# Revit family: STH7085_27
name_source: partatom
category: Luminárias
units: mm (PartAtom-declared; Revit-internal decimal feet)

## family parameters
Com base no plano de trabalho = Não
Compartilhado = Não
Corte com vazios quando carregada = Não
Cota do conector redondo = Utilizar diâmetro
Fonte luminosa = Sim
Manter orientação da anotação = Não
Ponto de cálculo do ambiente = Não
Sempre na vertical = Sim
Tipo de parte = Normal

## types (1)
- STH7085/27 - BIVOLT - 2700K - 700lm - 25°
    Altura = 0.1 m
    Arquivo de rede fotométrica = STELLA - STH7085-27 - PAR30 EVO 11W BDT.ies
    Cromado = Cromado
    Dimerização = 20-100%
    Diâmetro = 0.1 m
    Elevação padrão = 0 m
    Estrutura = Al - Branco
    Fabricante = Stella
    Filtro de cor = 16777215
    Fluxo Luminoso = 700 lm
    Grau de proteção (IP) = IP20
    IRC (Índice de reprodução de cores) = >90 (R9 >40)
    Luminoso = Luminoso - 2700K
    Modelo = Par30 EVO Dimerizável BDT
    Potência = 11 W
    Referência = STH7085/27 - BIVOLT
    Temperatura da cor (K) = 2700 K
    Tensão Elétrica = 100V-240V
    Troca de temperatura da cor de lâmpada com esmaecimento = <Nenhum>
    URL = https://stella.com.br
    Vidro = Vidro
    Ângulo de Abertura = 25°
    Ângulo de inclinação = 90.00°
